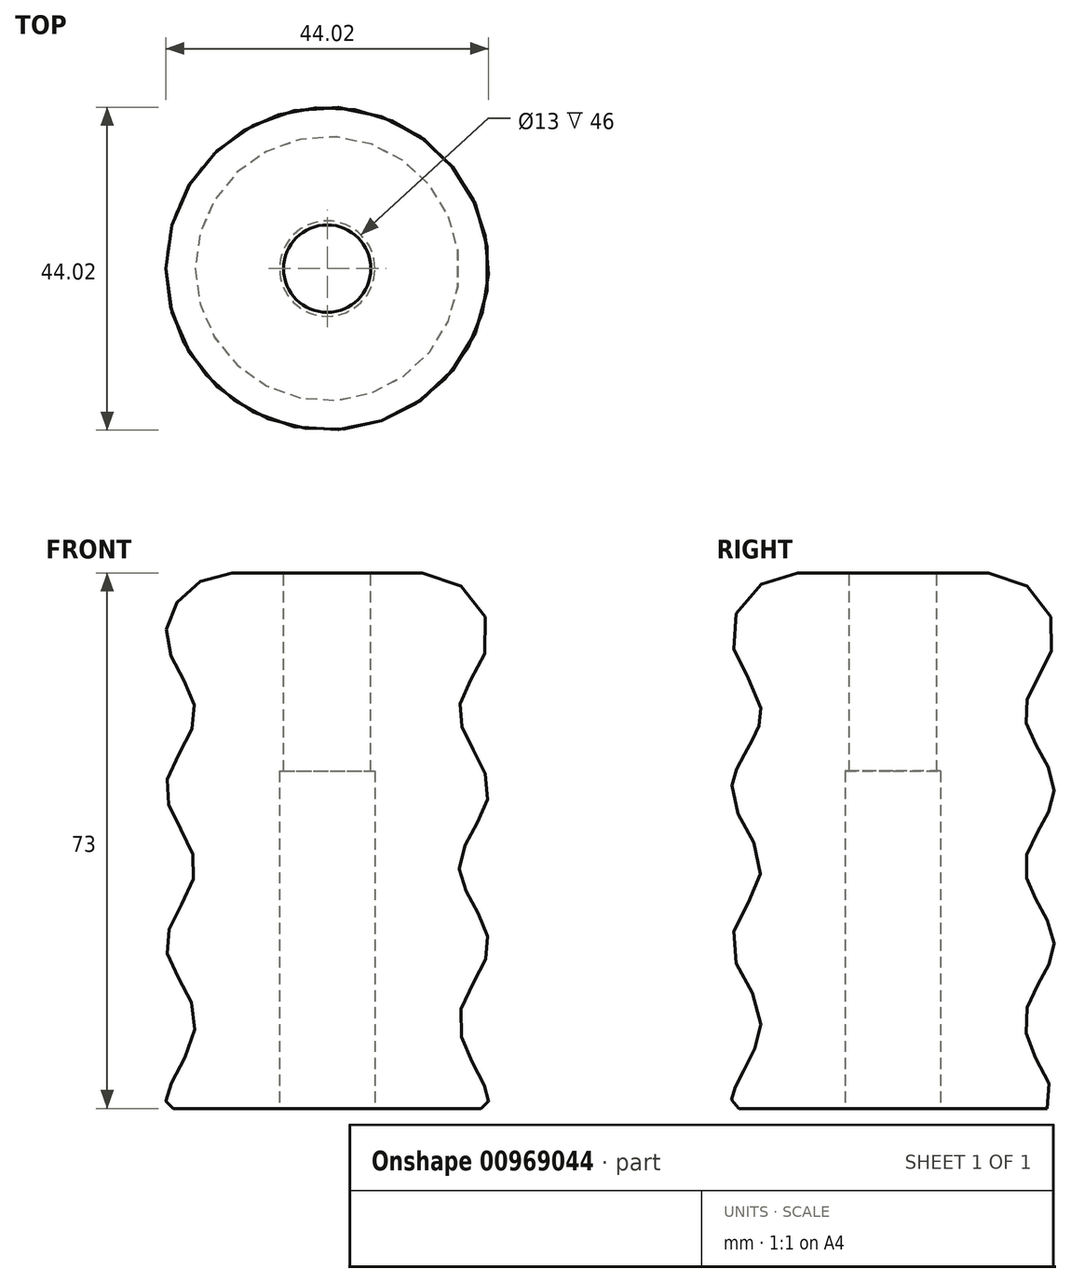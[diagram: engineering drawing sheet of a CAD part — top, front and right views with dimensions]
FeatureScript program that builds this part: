
annotation { "Feature Type Name" : "Feature", "Feature Type Description" : "" }
export const myFeature = defineFeature(function(context is Context, id is Id, definition is map)
    precondition{}
    {
        {
            var Q0;
            Q0=qCreatedBy(makeId("Right.planeOp"),FACE);
            var sketch = newSketch(context, id + "F0", { "sketchPlane" : qUnion([Q0])});
            skLineSegment(sketch, "E0.bottom", {"start": v(0, 0) * mm, "end": v(21, 0) * mm});
            skLineSegment(sketch, "E0.top", {"start": v(0, 73) * mm, "end": v(13, 73) * mm});
            skLineSegment(sketch, "E0.left", {"start": v(0, 0) * mm, "end": v(0, 73) * mm});
            skFitSpline(sketch, "E1", {"points": [v(13, 73) * mm, v(22, 64.4) * mm, v(18, 53.9) * mm, v(22, 43.4) * mm, v(18, 32.9) * mm, v(22, 22.4) * mm, v(18, 11.9) * mm, v(22, 1.4) * mm, v(21, 0) * mm], "startDerivative": vector(108.99, 0) * mm, "endDerivative": vector(-36.91, 0) * mm});
            skSolve(sketch);
        }
        {
            var Q0;
            Q0=qSketchRegion(id+"F0",true);
            var Q1;
            Q1=sQuery(id+"F0.wireOp",EDGE,"E0.left");
            revolve(context, id + "F1", {"surfaceOperationType" : NewSurfaceOperationType.NEW, "entities" : qUnion([Q0]), "axis" : qUnion([Q1]), "revolveType" : RevolveType.FULL});
        }
        {
            var Q0;
            Q0=makeQuery(id+"F1.opRevolve","SWEPT_FACE",FACE,{"disambiguationData":[OSD([sQuery(id+"F0.wireOp",EDGE,"E0.top")])]});
            var sketch = newSketch(context, id + "F2", { "sketchPlane" : qUnion([Q0])});
            skCircle(sketch, "E2", {"center": v(0, 0) * mm, "radius": 5.95 * mm});
            skSolve(sketch);
        }
        {
            var Q0;
            Q0=qSketchRegion(id+"F2",true);
            extrude(context, id + "F3", {"entities" : qUnion([Q0]), "operationType" : NewBodyOperationType.REMOVE, "endBound" : BoundingType.THROUGH_ALL, "oppositeDirection" : true, "depth" : 25 * mm, "offsetDistance" : 25 * mm});
        }
        {
            var Q0;
            Q0=makeQuery(id+"F1.opRevolve","SWEPT_FACE",FACE,{"disambiguationData":[OSD([sQuery(id+"F0.wireOp",EDGE,"E0.bottom")])]});
            var sketch = newSketch(context, id + "F4", { "sketchPlane" : qUnion([Q0])});
            skCircle(sketch, "E3", {"center": v(0, 0) * mm, "radius": 6.5 * mm});
            skSolve(sketch);
        }
        {
            var Q0;
            Q0=qSketchRegion(id+"F4",true);
            extrude(context, id + "F5", {"entities" : qUnion([Q0]), "operationType" : NewBodyOperationType.REMOVE, "oppositeDirection" : true, "depth" : 46 * mm, "offsetDistance" : 25 * mm});
        }
    });
